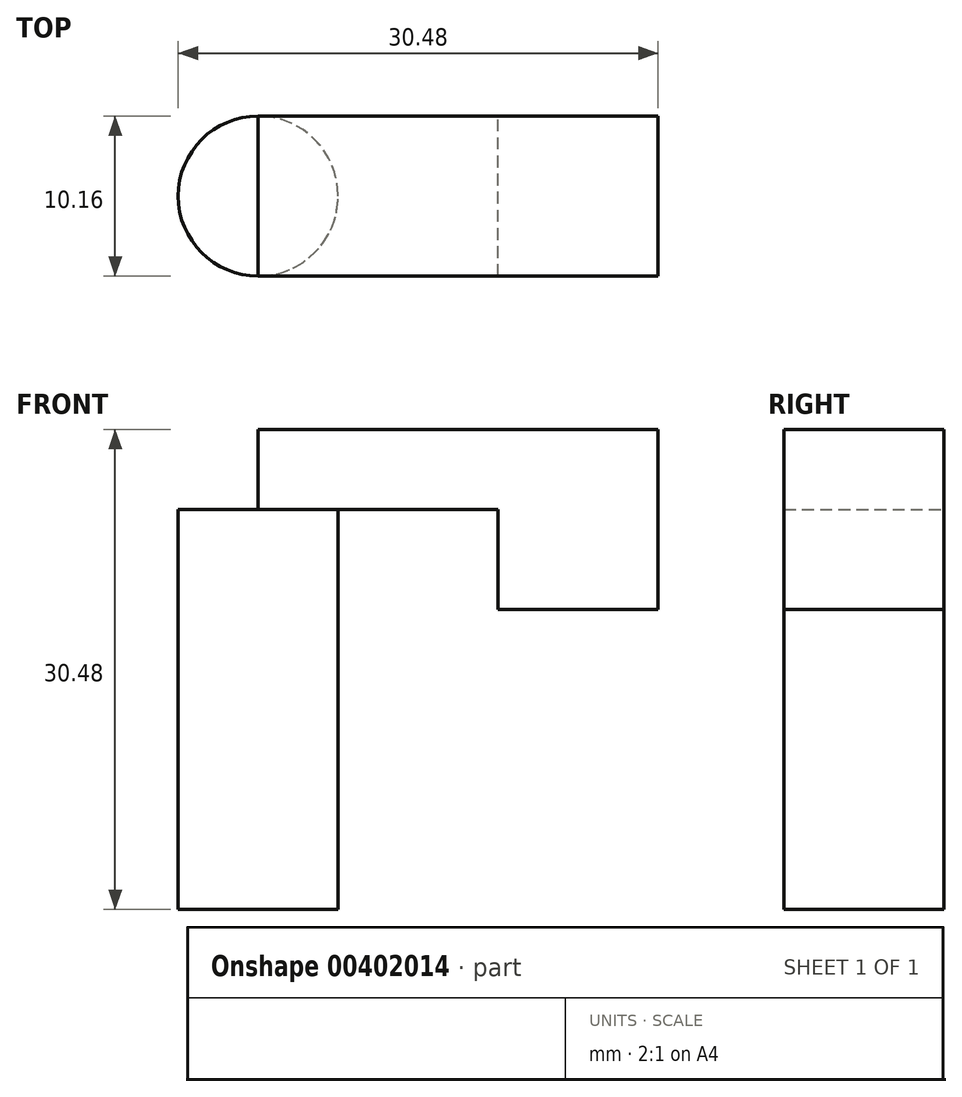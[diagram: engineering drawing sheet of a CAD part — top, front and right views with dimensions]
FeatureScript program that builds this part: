
annotation { "Feature Type Name" : "Feature", "Feature Type Description" : "" }
export const myFeature = defineFeature(function(context is Context, id is Id, definition is map)
    precondition{}
    {
        {
            var Q0;
            Q0=qCreatedBy(makeId("Top.planeOp"),FACE);
            var sketch = newSketch(context, id + "F0", { "sketchPlane" : qUnion([Q0])});
            skCircle(sketch, "E0", {"center": v(0, 0) * mm, "radius": 5.08 * mm});
            skSolve(sketch);
        }
        {
            var Q0;
            Q0 = qSketchRegion(id + "F0", true);
            extrude(context, id + "F1", {"entities" : qUnion([Q0]), "depth" : 25.4 * mm});
        }
        {
            var Q0;
            Q0=makeQuery(id+"F1.opExtrude","CAP_FACE",FACE,{"disambiguationData":[OSD([sQuery(id+"F0.wireOp",EDGE,"E0")])],"isStart":false});
            var sketch = newSketch(context, id + "F2", { "sketchPlane" : qUnion([Q0])});
            skLineSegment(sketch, "E1", {"start": v(0, -5.08) * mm, "end": v(25.4, -5.08) * mm});
            skLineSegment(sketch, "E2", {"start": v(25.4, -5.08) * mm, "end": v(25.4, 5.08) * mm});
            skLineSegment(sketch, "E3", {"start": v(25.4, 5.08) * mm, "end": v(0, 5.08) * mm});
            skLineSegment(sketch, "E4", {"start": v(0, 5.08) * mm, "end": v(0, -5.08) * mm});
            skSolve(sketch);
        }
        {
            var Q0;
            Q0 = qSketchRegion(id + "F2", true);
            extrude(context, id + "F3", {"entities" : qUnion([Q0]), "operationType" : NewBodyOperationType.ADD, "depth" : 5.08 * mm});
        }
        {
            var Q0;
            Q0=makeQuery(id+"F3.opExtrude","CAP_FACE",FACE,{"disambiguationData":[OSD([sQuery(id+"F2.wireOp",EDGE,"E1"),sQuery(id+"F2.wireOp",EDGE,"E2"),sQuery(id+"F2.wireOp",EDGE,"E3"),sQuery(id+"F2.wireOp",EDGE,"E4")])],"isStart":true});
            var sketch = newSketch(context, id + "F4", { "sketchPlane" : qUnion([Q0])});
            skLineSegment(sketch, "E5.bottom", {"start": v(25.4, 5.08) * mm, "end": v(15.24, 5.08) * mm});
            skLineSegment(sketch, "E5.top", {"start": v(25.4, -5.08) * mm, "end": v(15.24, -5.08) * mm});
            skLineSegment(sketch, "E5.left", {"start": v(25.4, 5.08) * mm, "end": v(25.4, -5.08) * mm});
            skLineSegment(sketch, "E5.right", {"start": v(15.24, 5.08) * mm, "end": v(15.24, -5.08) * mm});
            skSolve(sketch);
        }
        {
            var Q0;
            Q0 = qSketchRegion(id + "F4", true);
            extrude(context, id + "F5", {"entities" : qUnion([Q0]), "operationType" : NewBodyOperationType.ADD, "depth" : 6.35 * mm});
        }
    });
